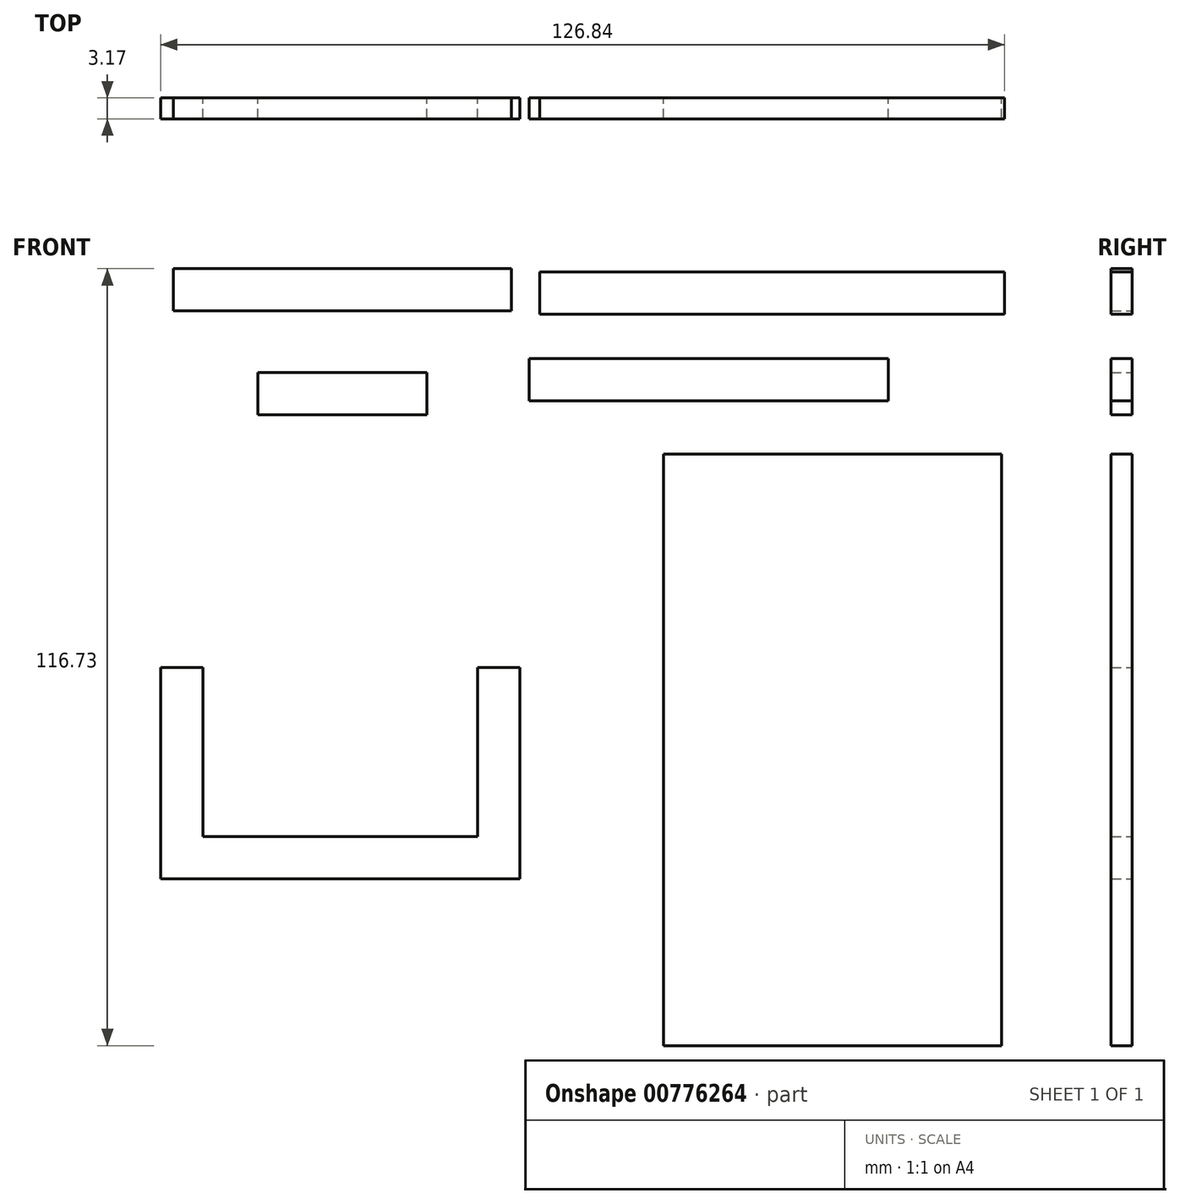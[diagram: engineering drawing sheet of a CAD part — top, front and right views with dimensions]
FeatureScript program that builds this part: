
annotation { "Feature Type Name" : "Feature", "Feature Type Description" : "" }
export const myFeature = defineFeature(function(context is Context, id is Id, definition is map)
    precondition{}
    {
        {
            var Q0;
            Q0=qCreatedBy(makeId("Front.planeOp"),FACE);
            var sketch = newSketch(context, id + "F0", { "sketchPlane" : qUnion([Q0])});
            skLineSegment(sketch, "E0.bottom", {"start": v(25.4, 44.45) * mm, "end": v(-25.4, 44.45) * mm});
            skLineSegment(sketch, "E0.top", {"start": v(25.4, -44.45) * mm, "end": v(-25.4, -44.45) * mm});
            skLineSegment(sketch, "E0.left", {"start": v(25.4, 44.45) * mm, "end": v(25.4, -44.45) * mm});
            skLineSegment(sketch, "E0.right", {"start": v(-25.4, 44.45) * mm, "end": v(-25.4, -44.45) * mm});
            skPoint(sketch, "E0.middle", {"position": v(0, 0) * mm});
            skSolve(sketch);
        }
        {
            var Q0;
            Q0=makeQuery(id+"F0.imprint","IMPRINT",FACE,{"disambiguationData":[TD([[makeQuery(id+"F0.imprint","IMPRINT",EDGE,{"derivedFrom":sQuery(id+"F0.wireOp",EDGE,"E0.bottom")}),1.0]])]});
            extrude(context, id + "F1", {"entities" : qUnion([Q0]), "depth" : 3.17 * mm, "offsetDistance" : 25.4 * mm});
        }
        {
            var Q0;
            Q0=qCreatedBy(makeId("Front.planeOp"),FACE);
            var sketch = newSketch(context, id + "F2", { "sketchPlane" : qUnion([Q0])});
            skLineSegment(sketch, "E1", {"start": v(-100.98, 12.35) * mm, "end": v(-94.63, 12.35) * mm});
            skLineSegment(sketch, "E2", {"start": v(-94.63, 12.35) * mm, "end": v(-94.63, -13.05) * mm});
            skLineSegment(sketch, "E3", {"start": v(-94.63, -13.05) * mm, "end": v(-53.36, -13.05) * mm});
            skLineSegment(sketch, "E4", {"start": v(-53.36, -13.05) * mm, "end": v(-53.36, 12.35) * mm});
            skLineSegment(sketch, "E5", {"start": v(-53.36, 12.35) * mm, "end": v(-47, 12.35) * mm});
            skLineSegment(sketch, "E6", {"start": v(-47, 12.35) * mm, "end": v(-47, -19.4) * mm});
            skLineSegment(sketch, "E7", {"start": v(-47, -19.4) * mm, "end": v(-100.98, -19.4) * mm});
            skLineSegment(sketch, "E8", {"start": v(-100.98, -19.4) * mm, "end": v(-100.98, 12.35) * mm});
            skSolve(sketch);
        }
        {
            var Q0;
            Q0=makeQuery(id+"F2.imprint","IMPRINT",FACE,{"disambiguationData":[TD([[makeQuery(id+"F2.imprint","IMPRINT",EDGE,{"derivedFrom":sQuery(id+"F2.wireOp",EDGE,"E1")}),-1.0]])]});
            extrude(context, id + "F3", {"entities" : qUnion([Q0]), "depth" : 3.17 * mm, "offsetDistance" : 25.4 * mm});
        }
        {
            var Q0;
            Q0=qCreatedBy(makeId("Front.planeOp"),FACE);
            var sketch = newSketch(context, id + "F4", { "sketchPlane" : qUnion([Q0])});
            skLineSegment(sketch, "E9.bottom", {"start": v(-48.28, 65.93) * mm, "end": v(-99.08, 65.93) * mm});
            skLineSegment(sketch, "E9.top", {"start": v(-48.28, 72.28) * mm, "end": v(-99.08, 72.28) * mm});
            skLineSegment(sketch, "E9.left", {"start": v(-48.28, 65.93) * mm, "end": v(-48.28, 72.28) * mm});
            skLineSegment(sketch, "E9.right", {"start": v(-99.08, 65.93) * mm, "end": v(-99.08, 72.28) * mm});
            skPoint(sketch, "E9.middle", {"position": v(-73.68, 69.1) * mm});
            skLineSegment(sketch, "E10.bottom", {"start": v(-60.98, 56.65) * mm, "end": v(-86.38, 56.65) * mm});
            skLineSegment(sketch, "E10.top", {"start": v(-60.98, 50.3) * mm, "end": v(-86.38, 50.3) * mm});
            skLineSegment(sketch, "E10.left", {"start": v(-60.98, 56.65) * mm, "end": v(-60.98, 50.3) * mm});
            skLineSegment(sketch, "E10.right", {"start": v(-86.38, 56.65) * mm, "end": v(-86.38, 50.3) * mm});
            skPoint(sketch, "E10.middle", {"position": v(-73.68, 53.47) * mm});
            skLineSegment(sketch, "E11.bottom", {"start": v(25.86, 71.78) * mm, "end": v(-43.99, 71.78) * mm});
            skLineSegment(sketch, "E11.top", {"start": v(25.86, 65.43) * mm, "end": v(-43.99, 65.43) * mm});
            skLineSegment(sketch, "E11.left", {"start": v(25.86, 71.78) * mm, "end": v(25.86, 65.43) * mm});
            skLineSegment(sketch, "E11.right", {"start": v(-43.99, 71.78) * mm, "end": v(-43.99, 65.43) * mm});
            skPoint(sketch, "E11.middle", {"position": v(-9.06, 68.6) * mm});
            skLineSegment(sketch, "E12.bottom", {"start": v(8.36, 52.4) * mm, "end": v(-45.61, 52.4) * mm});
            skLineSegment(sketch, "E12.top", {"start": v(8.36, 58.75) * mm, "end": v(-45.61, 58.75) * mm});
            skLineSegment(sketch, "E12.left", {"start": v(8.36, 52.4) * mm, "end": v(8.36, 58.75) * mm});
            skLineSegment(sketch, "E12.right", {"start": v(-45.61, 52.4) * mm, "end": v(-45.61, 58.75) * mm});
            skPoint(sketch, "E12.middle", {"position": v(-18.63, 55.57) * mm});
            skSolve(sketch);
        }
        {
            var Q0;
            Q0=makeQuery(id+"F4.imprint","IMPRINT",FACE,{"disambiguationData":[TD([[makeQuery(id+"F4.imprint","IMPRINT",EDGE,{"derivedFrom":sQuery(id+"F4.wireOp",EDGE,"E9.bottom")}),-1.0]])]});
            var Q1;
            Q1=makeQuery(id+"F4.imprint","IMPRINT",FACE,{"disambiguationData":[TD([[makeQuery(id+"F4.imprint","IMPRINT",EDGE,{"derivedFrom":sQuery(id+"F4.wireOp",EDGE,"E10.bottom")}),1.0]])]});
            var Q2;
            Q2=makeQuery(id+"F4.imprint","IMPRINT",FACE,{"disambiguationData":[TD([[makeQuery(id+"F4.imprint","IMPRINT",EDGE,{"derivedFrom":sQuery(id+"F4.wireOp",EDGE,"E12.bottom")}),-1.0]])]});
            var Q3;
            Q3=makeQuery(id+"F4.imprint","IMPRINT",FACE,{"disambiguationData":[TD([[makeQuery(id+"F4.imprint","IMPRINT",EDGE,{"derivedFrom":sQuery(id+"F4.wireOp",EDGE,"E11.bottom")}),1.0]])]});
            extrude(context, id + "F5", {"entities" : qUnion([Q0, Q1, Q2, Q3]), "depth" : 3.17 * mm, "offsetDistance" : 25.4 * mm});
        }
    });
